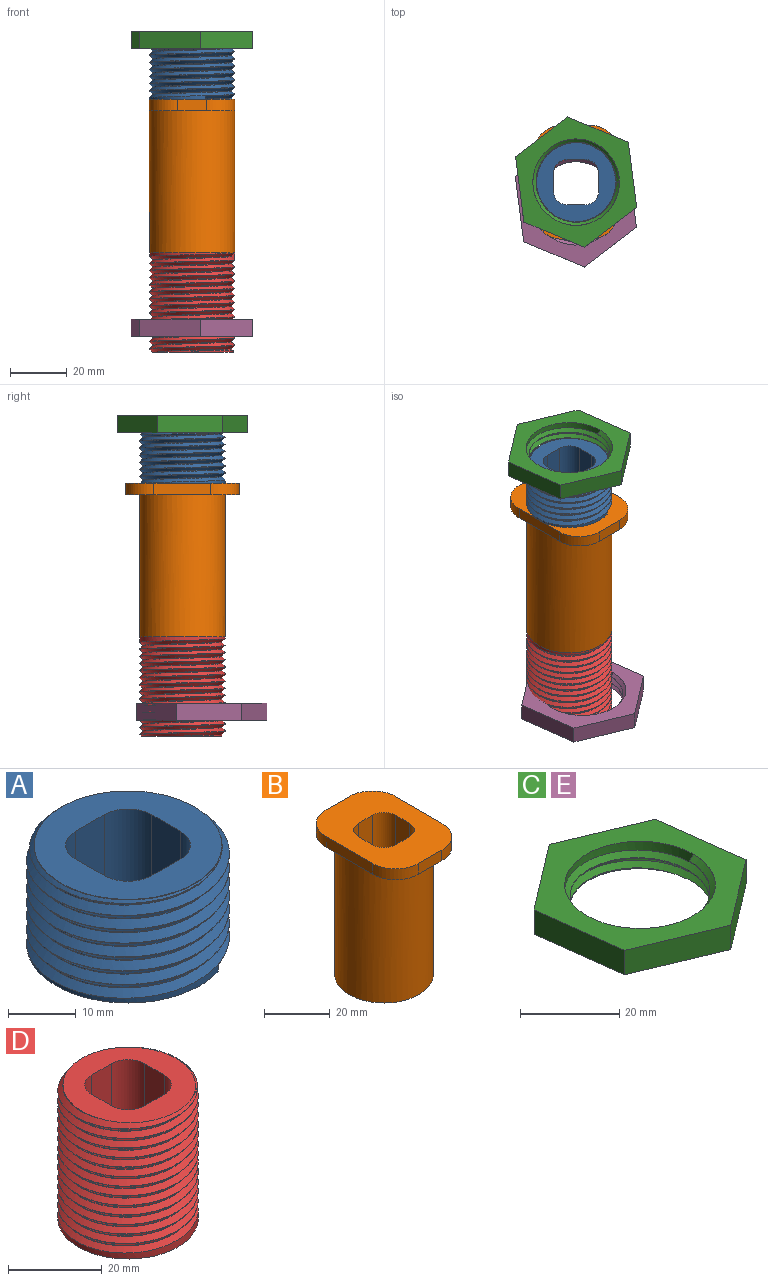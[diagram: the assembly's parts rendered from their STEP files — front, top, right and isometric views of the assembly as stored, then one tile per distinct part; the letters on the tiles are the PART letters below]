
ASSEMBLY  parts=5 mates=3
PART A: 17 faces, bbox 30.1x34.7x20.3 mm
  f0: cylinder r=15mm len=30mm, axis (0,0,-1), area -339.8mm2, adj f1,f3,f4,f6
  f1: bspline ~34.64x30.04mm, area 945.7mm2, adj f0,f4,f5,f16
  f2: plane 28.03x27.93mm, normal (0,0,1), area 372.5mm2, adj f5,f7,f8,f9,f10,f11,f12,f13
  f3: plane 29.98x29.35mm, normal (0,0,-1), area 446mm2, adj f0,f4,f5,f6,f7,f8,f9,f10
  f4: plane 1.21x1.06mm, normal (0.95,0.31,0.03), area 0.7mm2, adj f0,f1,f3,f5
  f5: bspline ~32.1x27.8mm, area 123.8mm2, adj f1,f2,f3,f4,f6,f15
  f6: bspline ~29.99x29.97mm, area 929.5mm2, adj f0,f3,f5,f16
  f7: plane 18x6mm, normal (0,-1,0), area 108mm2, adj f2,f3,f11,f14
  f8: plane 18x6mm, normal (1,0,0), area 108mm2, adj f2,f3,f11,f12
  f9: plane 18x6mm, normal (0,1,0), area 108mm2, adj f2,f3,f12,f13
  f10: plane 18x6mm, normal (-1,0,0), area 108mm2, adj f2,f3,f13,f14
  f11: cylinder r=5mm len=18mm, axis (0,0,1), area 141.4mm2, adj f2,f3,f7,f8
  f12: cylinder r=5mm len=18mm, axis (0,0,-1), area 141.4mm2, adj f2,f3,f8,f9
  f13: cylinder r=5mm len=18mm, axis (0,0,1), area 141.4mm2, adj f2,f3,f9,f10
  f14: cylinder r=5mm len=18mm, axis (0,0,-1), area 141.4mm2, adj f2,f3,f7,f10
  f15: revolved ~27.78x27.77mm, area 8.4mm2, adj f2,f5,f16
  f16: revolved ~29.98x29.96mm, area -66.6mm2, adj f1,f6,f15
PART B: 21 faces, bbox 30x40x54 mm
  f0: plane 30x30mm, normal (0,0,-1), area 472.3mm2, adj f2,f13,f14,f15,f16,f17,f18,f19
  f1: plane 40x30mm, normal (0,0,1), area 879.6mm2, adj f5,f6,f7,f8,f9,f10,f11,f12
  f2: cylinder r=15mm len=50mm, axis (0,0,-1), area 4712.4mm2, adj f0,f3,f4
  f3: plane 30x20mm, normal (0,0,-1), area 203.7mm2, adj f2,f5,f6,f7,f9,f10
  f4: plane 30x20mm, normal (0,0,-1), area 203.7mm2, adj f2,f5,f7,f8,f11,f12
  f5: plane 20x4mm, normal (1,0,0), area 80mm2, adj f1,f3,f4,f9,f12
  f6: plane 10x4mm, normal (0,1,0), area 40mm2, adj f1,f3,f9,f10
  f7: plane 20x4mm, normal (-1,0,0), area 80mm2, adj f1,f3,f4,f10,f11
  f8: plane 10x4mm, normal (0,-1,0), area 40mm2, adj f1,f4,f11,f12
  f9: cylinder r=10mm len=10mm, axis (0,0,1), area 62.8mm2, adj f1,f3,f5,f6
  f10: cylinder r=10mm len=10mm, axis (0,0,-1), area 62.8mm2, adj f1,f3,f6,f7
  f11: cylinder r=10mm len=10mm, axis (0,0,1), area 62.8mm2, adj f1,f4,f7,f8
  f12: cylinder r=10mm len=10mm, axis (0,0,-1), area 62.8mm2, adj f1,f4,f5,f8
  f13: plane 54x6mm, normal (1,0,0), area 324mm2, adj f0,f1,f17,f20
  f14: plane 54x6mm, normal (0,-1,0), area 324mm2, adj f0,f1,f17,f18
  f15: plane 54x6mm, normal (-1,0,0), area 324mm2, adj f0,f1,f18,f19
  f16: plane 54x6mm, normal (0,1,0), area 324mm2, adj f0,f1,f19,f20
  f17: cylinder r=5mm len=54mm, axis (0,0,-1), area 424.1mm2, adj f0,f1,f13,f14
  f18: cylinder r=5mm len=54mm, axis (0,0,1), area 424.1mm2, adj f0,f1,f14,f15
  f19: cylinder r=5mm len=54mm, axis (0,0,-1), area 424.1mm2, adj f0,f1,f15,f16
  f20: cylinder r=5mm len=54mm, axis (0,0,1), area 424.1mm2, adj f0,f1,f13,f16
PART C: 13 faces, bbox 43.6x46.7x8.3 mm
  f0: cylinder r=15.2mm len=30.4mm, axis (0,0,-1), area 133mm2, adj f7,f8,f9,f10,f12
  f1: plane 22.9x6mm, normal (-0.99,-0.13,0), area 138.6mm2, adj f2,f6,f7,f8
  f2: plane 21.31x8.89mm, normal (-0.39,-0.92,0), area 138.6mm2, adj f1,f3,f7,f8
  f3: plane 18.36x14.01mm, normal (0.61,-0.79,0), area 138.6mm2, adj f2,f4,f7,f8
  f4: plane 22.9x6mm, normal (0.99,0.13,0), area 138.6mm2, adj f3,f5,f7,f8
  f5: plane 21.31x8.89mm, normal (0.39,0.92,0), area 138.6mm2, adj f4,f6,f7,f8
  f6: plane 18.36x14.01mm, normal (-0.61,0.79,0), area 138.6mm2, adj f1,f5,f7,f8
  f7: plane 45.81x42.63mm, normal (0,0,1), area 659.8mm2, adj f0,f1,f2,f3,f4,f5,f6
  f8: plane 46.73x43.55mm, normal (0,0,-1), area 713mm2, adj f0,f1,f2,f3,f4,f5,f6,f10
  f9: plane 2.4x1.1mm, normal (0,1,0.03), area 1.4mm2, adj f0,f10,f11,f12
  f10: bspline ~35.1x30.4mm, area 312.5mm2, adj f0,f8,f9,f11
  f11: bspline ~32.56x28.24mm, area 34.1mm2, adj f8,f9,f10,f12
  f12: bspline ~35.1x30.47mm, area 237.3mm2, adj f0,f8,f9,f11
PART D: 16 faces, bbox 30.6x35.1x37 mm
  f0: plane 28.71x28.47mm, normal (0,0,1), area 388.3mm2, adj f5,f6,f7,f8,f9,f10,f11,f12
  f1: plane 30x30mm, normal (0,0,-1), area 472.3mm2, adj f2,f7,f8,f9,f10,f11,f12,f13
  f2: cylinder r=15mm len=34.53mm, axis (0,0,-1), area -229.4mm2, adj f1,f3,f4,f6,f15
  f3: plane 2.4x1.1mm, normal (0,1,0.03), area 1.4mm2, adj f2,f4,f5,f6
  f4: bspline ~34.64x34.43mm, area 1845.1mm2, adj f2,f3,f5,f15
  f5: bspline ~35.52x32.1mm, area 236.5mm2, adj f0,f3,f4,f6,f15
  f6: bspline ~36.1x34.64mm, area 1934.6mm2, adj f0,f2,f3,f5,f15
  f7: plane 35x6mm, normal (-1,0,0), area 210mm2, adj f0,f1,f11,f14
  f8: plane 35x6mm, normal (0,-1,0), area 210mm2, adj f0,f1,f11,f12
  f9: plane 35x6mm, normal (1,0,0), area 210mm2, adj f0,f1,f12,f13
  f10: plane 35x6mm, normal (0,1,0), area 210mm2, adj f0,f1,f13,f14
  f11: cylinder r=5mm len=35mm, axis (0,0,1), area 274.9mm2, adj f0,f1,f7,f8
  f12: cylinder r=5mm len=35mm, axis (0,0,-1), area 274.9mm2, adj f0,f1,f8,f9
  f13: cylinder r=5mm len=35mm, axis (0,0,1), area 274.9mm2, adj f0,f1,f9,f10
  f14: cylinder r=5mm len=35mm, axis (0,0,-1), area 274.9mm2, adj f0,f1,f7,f10
  f15: bspline ~30.2x16.63mm, area 33mm2, adj f0,f2,f4,f5,f6
PART E: same geometry as C
PLACE A t=(-144.9,12.29,43.99)mm
PLACE B t=(-144.9,12.29,-10.01)mm
PLACE C t=(-188.36,12.29,61.79)mm
PLACE D rot(axis=(1,0,0),180deg) t=(-144.9,12.29,-10.01)mm
PLACE E t=(-188.43,5.54,-39.36)mm
MATE fastened A.f0 <-> B.f2  axis (0,0,1) through (-144.9,12.29,43.99)mm
MATE cylindrical D.f2 <-> B.f2  axis (0,0,1) through (-144.9,12.29,-10.01)mm
MATE cylindrical C.f0 <-> B.f2  axis (0,0,1) through (-144.9,12.29,67.79)mm
